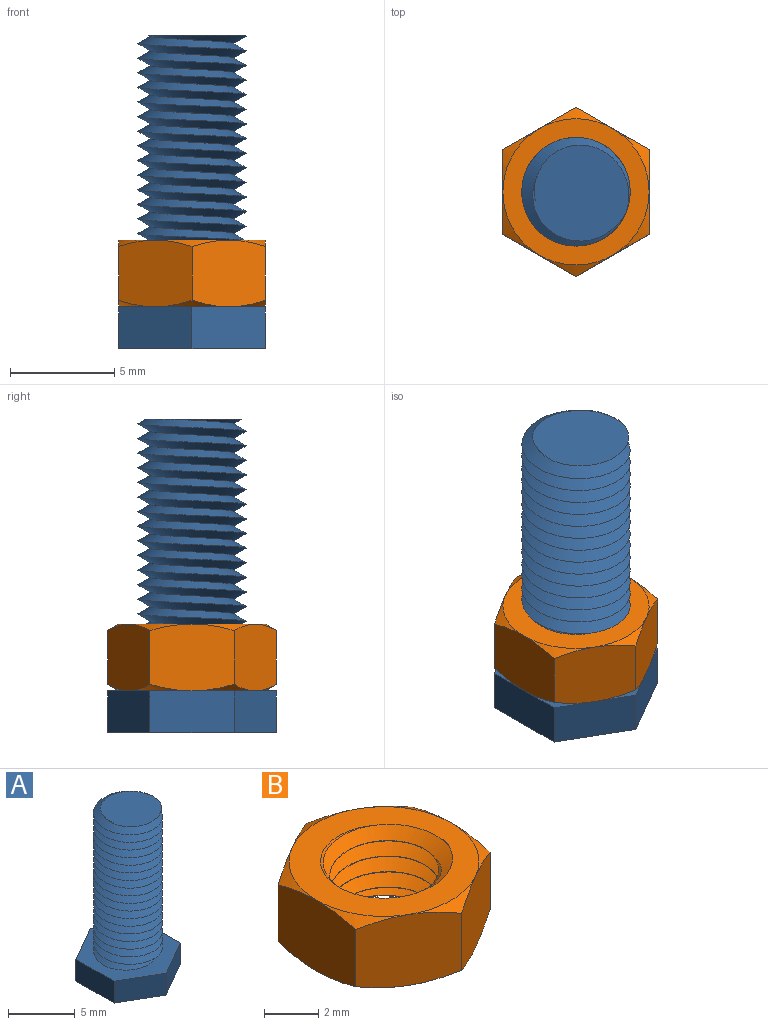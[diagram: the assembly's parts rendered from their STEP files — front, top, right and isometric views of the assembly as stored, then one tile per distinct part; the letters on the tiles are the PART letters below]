
ASSEMBLY  parts=2 mates=1
PART A: 18 faces, bbox 7.5x8.6x15.9 mm
  f0: cylinder r=2mm len=13mm, axis (0,0,-1), area 3.8mm2, adj f1,f2,f3,f4,f5,f6,f7,f8
  f1: plane 5.09x5.09mm, normal (0,0,1), area 16.6mm2, adj f0,f2,f3
  f2: bspline ~5.99x5.19mm, area 35.5mm2, adj f0,f1,f3,f8
  f3: bspline ~5.99x5.19mm, area 30.8mm2, adj f0,f1,f2,f9
  f4: bspline ~5.99x5.19mm, area 54mm2, adj f0,f5,f7,f10
  f5: bspline ~5.99x5.19mm, area 49.4mm2, adj f0,f4,f6,f10
  f6: bspline ~5.99x5.19mm, area 49.5mm2, adj f0,f5,f7,f8
  f7: bspline ~5.99x5.19mm, area 49.5mm2, adj f0,f4,f6,f9
  f8: bspline ~5.99x5.19mm, area 49.5mm2, adj f0,f2,f6,f9
  f9: bspline ~5.99x5.19mm, area 49.5mm2, adj f0,f3,f7,f8
  f10: plane 8.56x7.47mm, normal (0,0,1), area 25.9mm2, adj f0,f4,f5,f11,f12,f13,f14,f15
  f11: plane 4.04x2mm, normal (1,0,0), area 8.1mm2, adj f10,f12,f16,f17
  f12: plane 3.5x2.02mm, normal (0.5,0.87,0), area 8.1mm2, adj f10,f11,f13,f17
  f13: plane 3.5x2.02mm, normal (-0.5,0.87,0), area 8.1mm2, adj f10,f12,f14,f17
  f14: plane 4.04x2mm, normal (-1,0,0), area 8.1mm2, adj f10,f13,f15,f17
  f15: plane 3.5x2.02mm, normal (-0.5,-0.87,0), area 8.1mm2, adj f10,f14,f16,f17
  f16: plane 3.5x2.02mm, normal (0.5,-0.87,0), area 8.1mm2, adj f10,f11,f15,f17
  f17: plane 8.08x7mm, normal (0,0,-1), area 42.4mm2, adj f11,f12,f13,f14,f15,f16
PART B: 25 faces, bbox 8.4x8.4x4.4 mm
  f0: plane 3.83x3.54mm, normal (0.5,-0.87,0), area 12.1mm2, adj f1,f5,f13,f14,f15,f16
  f1: plane 4.38x3.54mm, normal (1,0,0), area 12.1mm2, adj f0,f2,f9,f14,f15,f20
  f2: plane 3.83x3.54mm, normal (0.5,0.87,0), area 12.1mm2, adj f1,f3,f9,f10,f19,f20
  f3: plane 3.83x3.54mm, normal (-0.5,0.87,0), area 12.1mm2, adj f2,f4,f10,f11,f18,f19
  f4: plane 4.38x3.54mm, normal (-1,0,0), area 12.1mm2, adj f3,f5,f11,f12,f17,f18
  f5: plane 3.83x3.54mm, normal (-0.5,-0.87,0), area 12.1mm2, adj f0,f4,f12,f13,f16,f17
  f6: plane 7.12x7.12mm, normal (0,0,-1), area 20.5mm2, adj f15,f16,f17,f18,f19,f20,f22,f23
  f7: plane 7.1x7.1mm, normal (0,0,1), area 20.5mm2, adj f9,f10,f11,f12,f13,f14,f21,f23
  f8: cylinder r=2mm len=4mm, axis (0,0,-1), area 0.4mm2, adj f21,f22,f23,f24
  f9: cone r=3.5mm half-angle=60deg, axis (0,0,-1), area 1.2mm2, adj f1,f2,f7
  f10: cone r=3.5mm half-angle=60deg, axis (0,0,-1), area 1.2mm2, adj f2,f3,f7
  f11: cone r=3.5mm half-angle=60deg, axis (0,0,-1), area 1.2mm2, adj f3,f4,f7
  f12: cone r=3.5mm half-angle=60deg, axis (0,0,-1), area 1.2mm2, adj f4,f5,f7
  f13: cone r=3.5mm half-angle=60deg, axis (0,0,-1), area 1.2mm2, adj f0,f5,f7
  f14: cone r=3.5mm half-angle=60deg, axis (0,0,-1), area 1.2mm2, adj f0,f1,f7
  f15: cone r=3.5mm half-angle=60deg, axis (0,0,1), area 1.2mm2, adj f0,f1,f6
  f16: cone r=3.5mm half-angle=60deg, axis (0,0,1), area 1.2mm2, adj f0,f5,f6
  f17: cone r=3.5mm half-angle=60deg, axis (0,0,1), area 1.2mm2, adj f4,f5,f6
  f18: cone r=3.5mm half-angle=60deg, axis (0,0,1), area 1.2mm2, adj f3,f4,f6
  f19: cone r=3.5mm half-angle=60deg, axis (0,0,1), area 1.2mm2, adj f2,f3,f6
  f20: cone r=3.5mm half-angle=60deg, axis (0,0,1), area 1.2mm2, adj f1,f2,f6
  f21: cone r=2mm half-angle=45deg, axis (0,0,1), area 2mm2, adj f7,f8,f23,f24
  f22: cone r=2.34mm half-angle=45deg, axis (0,0,-1), area 2mm2, adj f6,f8,f23,f24
  f23: bspline ~5.99x5.19mm, area 42.7mm2, adj f6,f7,f8,f21,f22,f24
  f24: bspline ~5.99x5.19mm, area 42.7mm2, adj f6,f7,f8,f21,f22,f23
PLACE A at identity fixed
PLACE B at identity
MATE cylindrical A.f0 <-> B.f8  axis (0,0,1) through (0,0,0)mm
